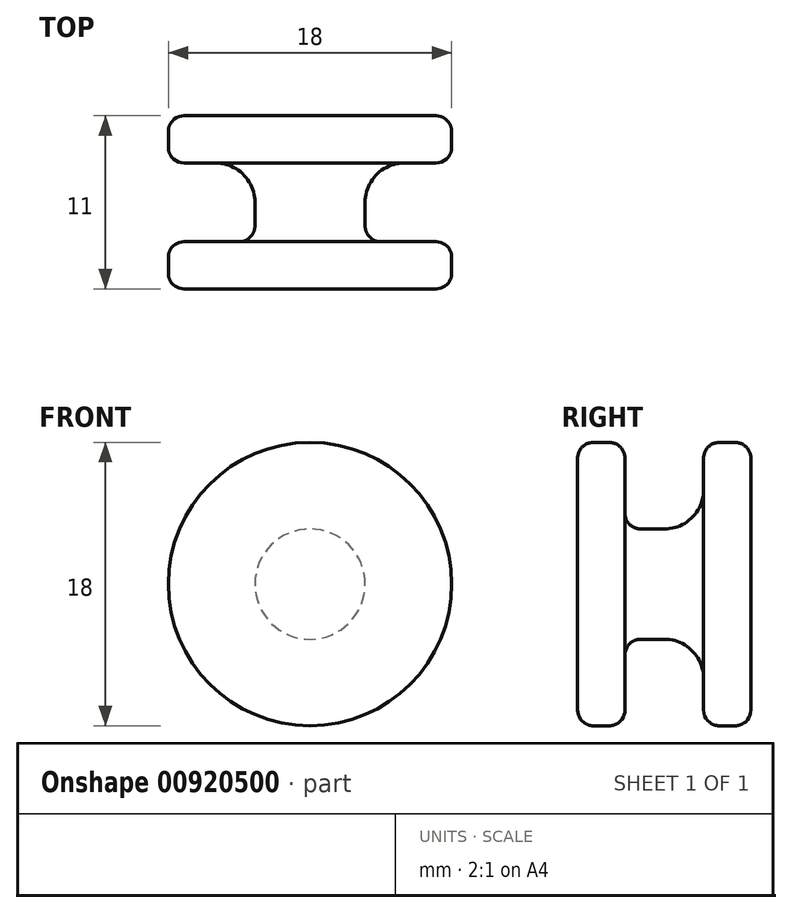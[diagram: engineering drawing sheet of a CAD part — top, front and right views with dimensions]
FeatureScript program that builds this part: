
annotation { "Feature Type Name" : "Feature", "Feature Type Description" : "" }
export const myFeature = defineFeature(function(context is Context, id is Id, definition is map)
    precondition{}
    {
        {
            var Q0;
            Q0=qCreatedBy(makeId("Top.planeOp"),FACE);
            var sketch = newSketch(context, id + "F0", { "sketchPlane" : qUnion([Q0])});
            skLineSegment(sketch, "E0", {"start": v(0, 0) * mm, "end": v(8, 0) * mm});
            skLineSegment(sketch, "E1", {"start": v(9, 1) * mm, "end": v(9, 2) * mm});
            skLineSegment(sketch, "E2", {"start": v(8, 3) * mm, "end": v(4.5, 3) * mm});
            skLineSegment(sketch, "E3", {"start": v(3.5, 4) * mm, "end": v(3.5, 5.5) * mm});
            skLineSegment(sketch, "E4", {"start": v(6, 8) * mm, "end": v(8, 8) * mm});
            skLineSegment(sketch, "E5", {"start": v(9, 9) * mm, "end": v(9, 10) * mm});
            skLineSegment(sketch, "E6", {"start": v(8, 11) * mm, "end": v(0, 11) * mm});
            skLineSegment(sketch, "E7", {"start": v(0, 11) * mm, "end": v(0, 0) * mm});
            skPoint(sketch, "E8.visualSharp", {"position": v(3.5, 8) * mm});
            skArc(sketch, "E8.filletArc", {"start": v(6, 8) * mm, "mid": v(4.23, 7.27) * mm, "end": v(3.5, 5.5) * mm});
            skPoint(sketch, "E9.visualSharp", {"position": v(3.5, 3) * mm});
            skArc(sketch, "E9.filletArc", {"start": v(3.5, 4) * mm, "mid": v(3.8, 3.3) * mm, "end": v(4.5, 3) * mm});
            skPoint(sketch, "E10.visualSharp", {"position": v(9, 8) * mm});
            skArc(sketch, "E10.filletArc", {"start": v(8, 8) * mm, "mid": v(8.7, 8.3) * mm, "end": v(9, 9) * mm});
            skPoint(sketch, "E11.visualSharp", {"position": v(9, 3) * mm});
            skArc(sketch, "E11.filletArc", {"start": v(9, 2) * mm, "mid": v(8.7, 2.7) * mm, "end": v(8, 3) * mm});
            skPoint(sketch, "E12.visualSharp", {"position": v(9, 11) * mm});
            skArc(sketch, "E12.filletArc", {"start": v(9, 10) * mm, "mid": v(8.7, 10.7) * mm, "end": v(8, 11) * mm});
            skPoint(sketch, "E13.visualSharp", {"position": v(9, 0) * mm});
            skArc(sketch, "E13.filletArc", {"start": v(8, 0) * mm, "mid": v(8.7, 0.3) * mm, "end": v(9, 1) * mm});
            skSolve(sketch);
        }
        {
            var Q0;
            Q0=makeQuery(id+"F0.imprint","IMPRINT",FACE,{"disambiguationData":[TD([[makeQuery(id+"F0.imprint","IMPRINT",EDGE,{"derivedFrom":sQuery(id+"F0.wireOp",EDGE,"E0")}),1.0]])]});
            var Q1;
            Q1=sQuery(id+"F0.wireOp",EDGE,"E12.filletArc");
            var Q2;
            Q2=sQuery(id+"F0.wireOp",EDGE,"E6");
            var Q3;
            Q3=sQuery(id+"F0.wireOp",EDGE,"E5");
            var Q4;
            Q4=sQuery(id+"F0.wireOp",EDGE,"E10.filletArc");
            var Q5;
            Q5=sQuery(id+"F0.wireOp",EDGE,"E8.filletArc");
            var Q6;
            Q6=sQuery(id+"F0.wireOp",EDGE,"E3");
            var Q7;
            Q7=sQuery(id+"F0.wireOp",EDGE,"E9.filletArc");
            var Q8;
            Q8=sQuery(id+"F0.wireOp",EDGE,"E2");
            var Q9;
            Q9=sQuery(id+"F0.wireOp",EDGE,"E11.filletArc");
            var Q10;
            Q10=sQuery(id+"F0.wireOp",EDGE,"E1");
            var Q11;
            Q11=sQuery(id+"F0.wireOp",EDGE,"E13.filletArc");
            var Q12;
            Q12=sQuery(id+"F0.wireOp",EDGE,"E0");
            var Q13;
            Q13=sQuery(id+"F0.wireOp",EDGE,"E7");
            revolve(context, id + "F1", {"surfaceOperationType" : NewSurfaceOperationType.NEW, "entities" : qUnion([Q0]), "surfaceEntities" : qUnion([Q1, Q2, Q3, Q4, Q5, Q6, Q7, Q8, Q9, Q10, Q11, Q12]), "axis" : qUnion([Q13]), "revolveType" : RevolveType.FULL});
        }
    });
